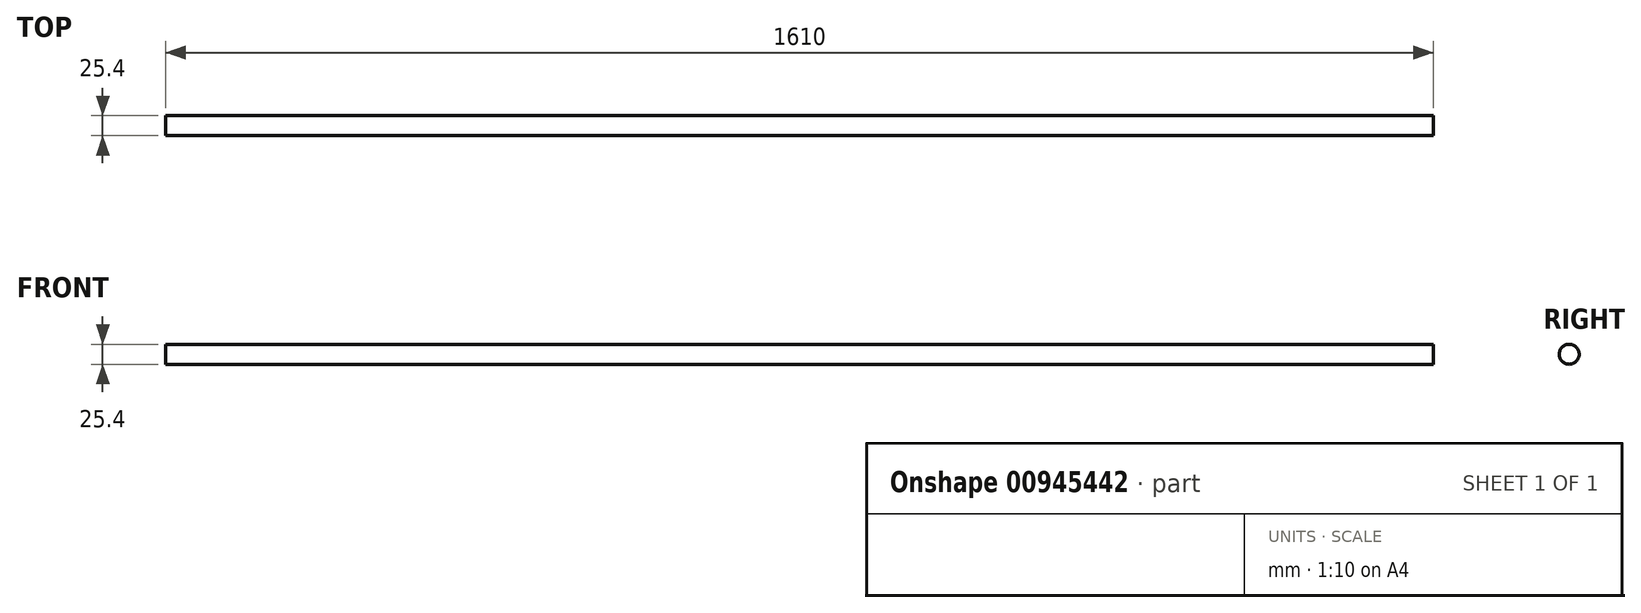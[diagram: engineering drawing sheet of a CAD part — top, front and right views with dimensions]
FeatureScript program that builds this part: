
annotation { "Feature Type Name" : "Feature", "Feature Type Description" : "" }
export const myFeature = defineFeature(function(context is Context, id is Id, definition is map)
    precondition{}
    {
        {
            var Q0;
            Q0=qCreatedBy(makeId("Right.planeOp"),FACE);
            var sketch = newSketch(context, id + "F0", { "sketchPlane" : qUnion([Q0])});
            skCircle(sketch, "E0", {"center": v(0, 0) * mm, "radius": 12.7 * mm});
            skSolve(sketch);
        }
        {
            var Q0;
            Q0=sQuery(id+"F0.wireOp",EDGE,"E0");
            extrude(context, id + "F1", {"bodyType" : ToolBodyType.SURFACE, "surfaceEntities" : qUnion([Q0]), "depth" : 1610 * mm, "offsetDistance" : 25.4 * mm});
        }
    });
